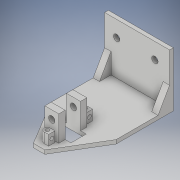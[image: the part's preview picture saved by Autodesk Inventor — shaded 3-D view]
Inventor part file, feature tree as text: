
AUTODESK INVENTOR PART (.ipt)
format: ipt  version: 2019 (Build 230136000, 136)  size: 273,408 bytes
history: native  units: in
note: dims shown in document units (in); Inventor stores cm internally (conversion verified against a paired STEP export)
features: sketch x15, extrude x7, hole x5, loft x3, plane x1, other x1
ambient origin geometry x8: Origin, YZ Plane, XZ Plane, XY Plane, X Axis, Y Axis, Z Axis, Center Point
bodies: Solid1 (feature_tree)
feature tree (32):
  extrude  "Extrusion1"  Depth=1.5748in
  extrude  "Extrusion2"  Depth=0.1969in
  loft  "Loft1"
  loft  "Loft2"
  plane  "Work Plane1"
  loft  "Loft3"
  sketch  "Sketch8"  dims[d19=0.1969in d20=0.6299in]
  extrude  "Extrusion3"  Depth=0.3543in
  hole  "Hole1"  [1 undecoded]
  hole  "Hole2"  [1 undecoded]
  extrude  "Extrusion4"  Depth=0.1969in
  extrude  "Extrusion5"  TaperAngle=0.0deg  [1 undecoded]
  extrude  "Extrusion6"  Depth=0.6299in
  hole  "Hole3"  [1 undecoded]
  sketch  "Sketch14"  dims[d33=0.1969in d34=0.3543in]
  extrude  "Extrusion7"  Depth=0.3543in
  hole  "Hole4"  [1 undecoded]
  hole  "Hole5"  [1 undecoded]
  sketch  "Sketch1"  dims[d0=2.0079in d1=1.5748in]
  sketch  "Sketch2"  dims[d2=2.0079in d5=0.1969in]
  sketch  "Sketch3"  dims[d7=0.1969in d8=0.1181in d9=0.0in]
  sketch  "Sketch4"  dims[d10=1.7717in d11=2.0079in]
  sketch  "Sketch5"  dims[d12=1.7717in d13=2.0079in]
  sketch  "Sketch6"  dims[d14=0.1181in d15=0.0in d16=0.3543in]
  sketch  "Sketch7"  dims[d17=0.1969in d18=0.3543in]
  other  "Edges1"
  sketch  "Sketch9"  dims[d21=0.1969in d22=0.6299in]
  sketch  "Sketch10"  dims[d23=0.1969in d24=0.0in d25=90.0deg]
  sketch  "Sketch11"  dims[d26=0.0in d27=90.0deg d28=0.6299in]
  sketch  "Sketch12"  dims[d29=0.1969in d30=0.6299in]
  sketch  "Sketch13"  dims[d31=0.1969in d32=0.3543in]
  sketch  "Sketch15"  dims[d35=0.1969in d36=0.0in d37=90.0deg d38=0.0in d39=90.0deg d40=1.378in d41=0.8268in d42=0.1181in d43=0.3543in d44=0.1181in d45=0.3543in d46=0.0in d47=90.0deg d48=0.0in d49=90.0deg d50=0.8661in d51=0.0591in d52=0.1378in d53=0.2362in d54=0.1969in d55=0.2362in d56=0.0984in d57=0.315in d58=0.0in d59=0.1181in d60=0.2362in d61=0.1575in d62=0.0787in d63=90.0deg d64=0.315in d65=0.8108in d66=0.1181in d67=0.1181in d68=0.2362in d69=0.1575in d70=0.0787in d71=90.0deg d72=0.315in d73=0.0in d74=0.7874in d76=0.4331in d77=0.1969in d78=0.4331in d79=0.1969in d80=0.7874in d81=0.0in d82=0.1772in d83=0.4331in d84=0.1772in d85=0.4724in d86=0.7874in d87=0.4724in d88=0.1181in d89=0.0in d90=0.4724in d91=0.1969in d92=0.4331in d93=0.1969in d94=0.4331in d95=0.7874in d96=0.0in d99=0.1969in d100=0.1969in d101=0.2362in d102=0.1575in d103=0.0787in d104=90.0deg d105=0.8661in d106=0.0in d107=0.9646in d108=0.2362in d109=0.1969in d110=0.2362in d111=0.1969in d112=0.0984in d113=0.315in d114=0.0in d115=0.1181in d116=0.2362in d117=0.1575in d118=0.0787in d119=90.0deg d120=0.8661in d121=0.0in d122=0.1181in d123=0.1181in d124=0.2362in d125=0.1575in d126=0.0787in d127=90.0deg d128=0.8661in d129=0.0in]
note: 6 required parameter values undecoded (feature->parameter linkage not recoverable at this tier; creation-order binding heuristic only, values carry confidence <= 0.55)
